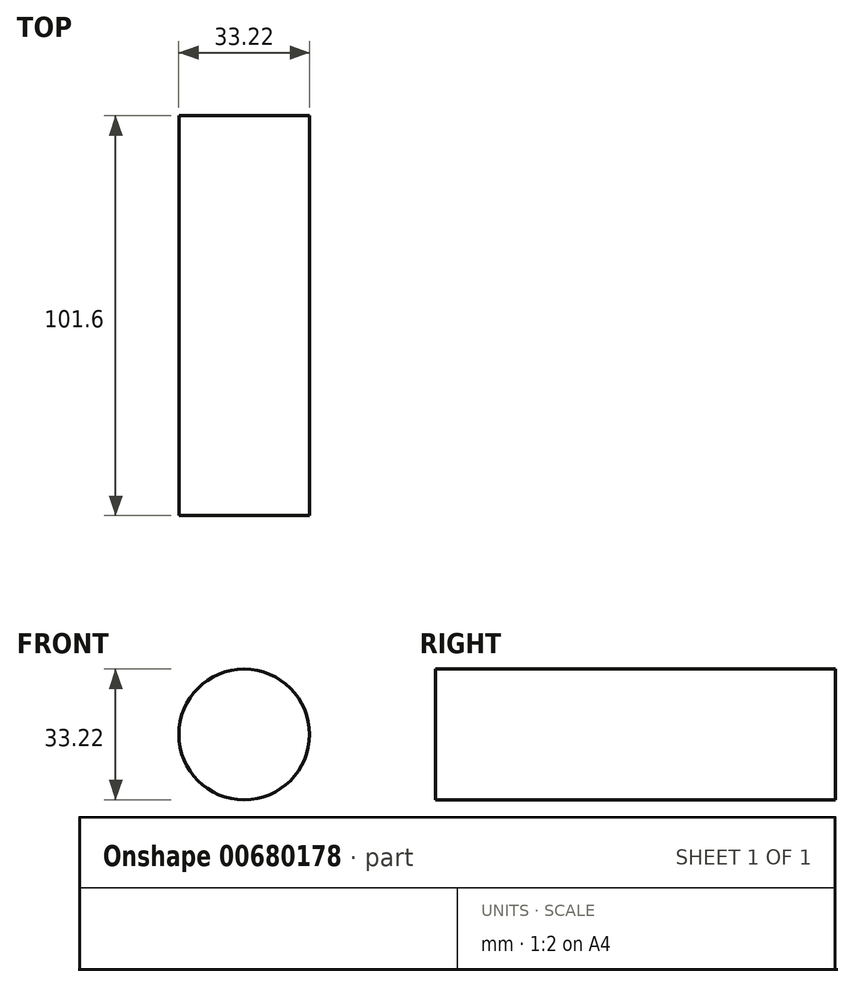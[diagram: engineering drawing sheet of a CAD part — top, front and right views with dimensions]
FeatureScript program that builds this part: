
annotation { "Feature Type Name" : "Feature", "Feature Type Description" : "" }
export const myFeature = defineFeature(function(context is Context, id is Id, definition is map)
    precondition{}
    {
        {
            var Q0;
            Q0=qCreatedBy(makeId("Front.planeOp"),FACE);
            var sketch = newSketch(context, id + "F0", { "sketchPlane" : qUnion([Q0])});
            skCircle(sketch, "E0", {"center": v(0, -2.2) * mm, "radius": 16.6 * mm});
            skSolve(sketch);
        }
        {
            var Q0;
            Q0 = qSketchRegion(id + "F0", true);
            extrude(context, id + "F1", {"entities" : qUnion([Q0]), "depth" : 101.6 * mm, "offsetDistance" : 25.4 * mm});
        }
    });
